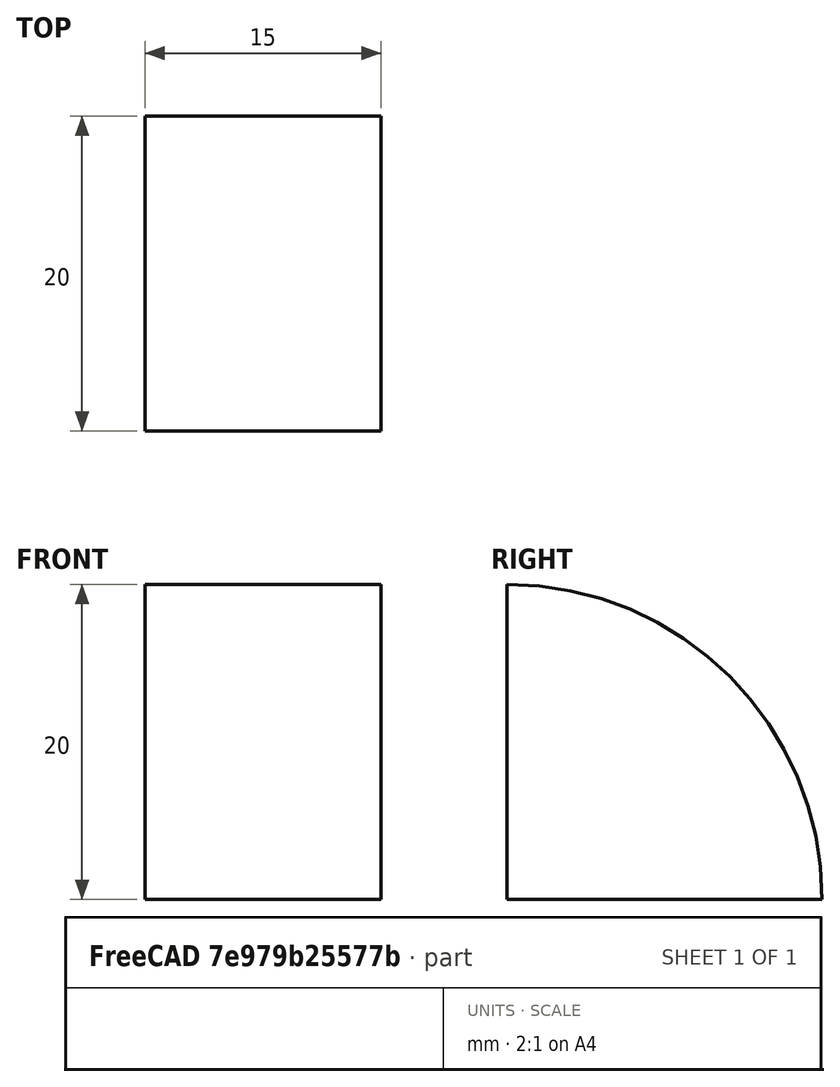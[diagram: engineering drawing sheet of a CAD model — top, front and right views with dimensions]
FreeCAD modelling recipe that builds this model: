
FCSTD DOCUMENT  (FreeCAD 1.0R38641 +468 (Git))
Label: stopper-arc
License: All rights reserved
LicenseURL: https://en.wikipedia.org/wiki/All_rights_reserved
objects: Sketcher::SketchObject×1, PartDesign::Pad×1, PartDesign::Body×1
note: 6 computed .brp shape members not serialized (recipe doc carries the construction recipe); baked Part::Feature solids carry a one-line shape summary decoded from their .brp

FEATURE [Sketcher::SketchObject] Sketch
  ArcFitTolerance = 1e-06
  AttachmentSupport = -> [YZ_Plane]
  FullyConstrained = false
  MakeInternals = false
  MapMode = 5
  Placement = pos=(0,0,0) rot=(0.57735,0.57735,0.57735;2.0944rad)
  sketch-geometry (3):
    g0: ArcOfCircle CenterX=-10 CenterY=-5.79791 CenterZ=0 NormalX=0 NormalY=0 NormalZ=1 AngleXU=0 Radius=20 StartAngle=0 EndAngle=1.5708
    g1: LineSegment StartX=-9.99999 StartY=14.2021 StartZ=0 EndX=-10 EndY=-5.79791 EndZ=0
    g2: LineSegment StartX=-10 StartY=-5.79791 StartZ=0 EndX=10 EndY=-5.79791 EndZ=0
  constraints (6):
    c: Radius(g0) = 20
    c: Angle(g0) = 1.5708
    c: Coincident(g0,g1)
    c: Coincident(g2,g0)
    c: Coincident(g2,g0)
    c: Horizontal(g2)
FEATURE [PartDesign::Pad] Pad
  Direction = (1,0,0)
  Length = 15
  Length2 = 10
  Placement = pos=(0,0,0) rot=(1,1,1;2.0944rad)
  Profile = -> Sketch
  ReferenceAxis = -> Sketch [N_Axis]
  Refine = true
  Suppressed = false
  Type = 0
FEATURE [PartDesign::Body] Body
  AllowCompound = false
  Group = -> [Sketch,Pad]
  Origin = -> Origin
  Tip = -> Pad
